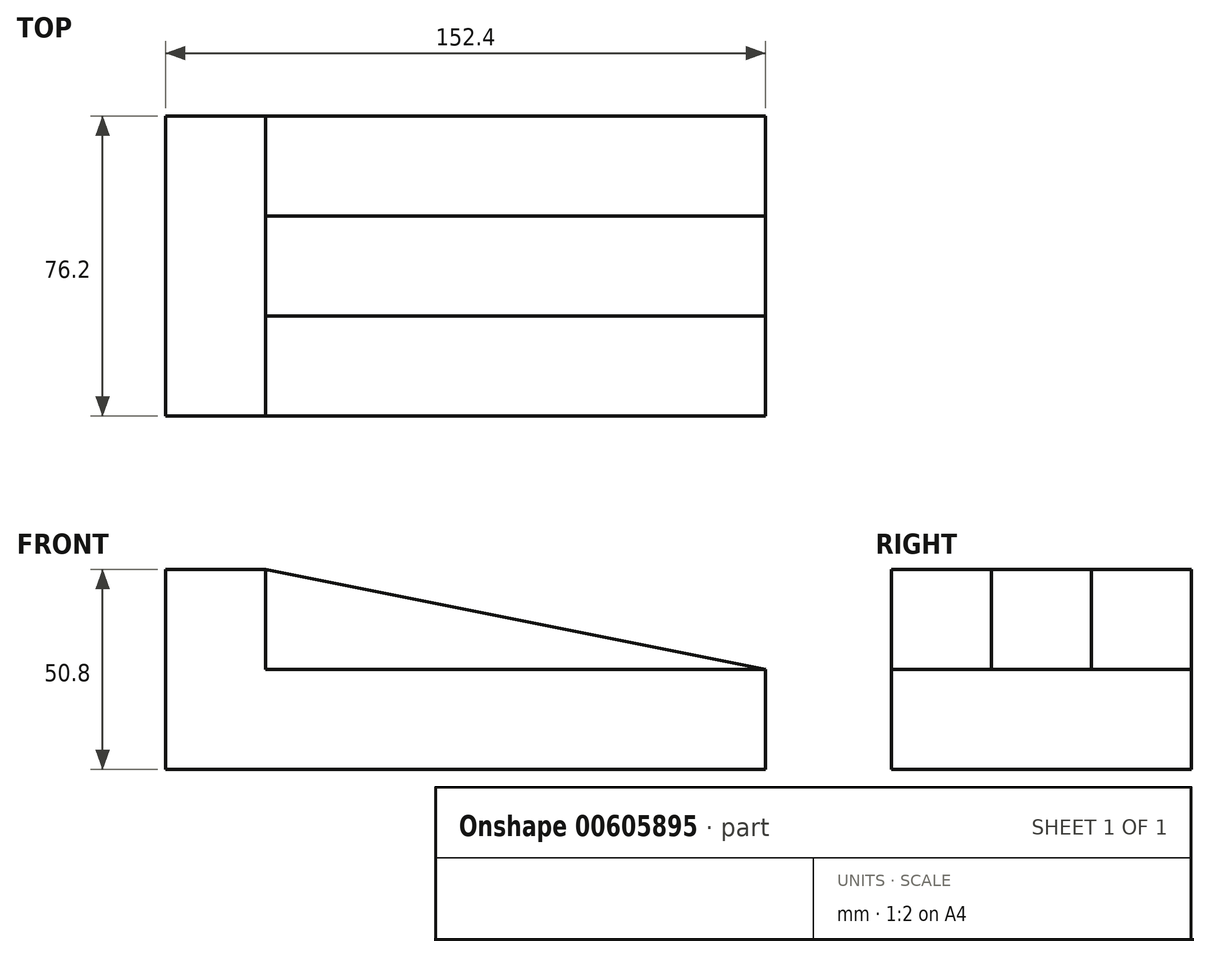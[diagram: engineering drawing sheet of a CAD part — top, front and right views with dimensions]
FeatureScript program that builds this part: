
annotation { "Feature Type Name" : "Feature", "Feature Type Description" : "" }
export const myFeature = defineFeature(function(context is Context, id is Id, definition is map)
    precondition{}
    {
        {
            var Q0;
            Q0=qCreatedBy(makeId("Front.planeOp"),FACE);
            var sketch = newSketch(context, id + "F0", { "sketchPlane" : qUnion([Q0])});
            skLineSegment(sketch, "E0", {"start": v(0, 0) * mm, "end": v(0, 50.8) * mm});
            skLineSegment(sketch, "E1", {"start": v(0, 0) * mm, "end": v(152.4, 0) * mm});
            skLineSegment(sketch, "E2", {"start": v(152.4, 0) * mm, "end": v(152.4, 50.8) * mm});
            skLineSegment(sketch, "E3", {"start": v(152.4, 50.8) * mm, "end": v(0, 50.8) * mm});
            skSolve(sketch);
        }
        {
            var Q0;
            Q0=makeQuery(id+"F0.imprint","IMPRINT",FACE,{"disambiguationData":[TD([[makeQuery(id+"F0.imprint","IMPRINT",EDGE,{"derivedFrom":sQuery(id+"F0.wireOp",EDGE,"E0")}),-1.0]])]});
            extrude(context, id + "F1", {"entities" : qUnion([Q0]), "depth" : 76.2 * mm, "offsetDistance" : 25.4 * mm});
        }
        {
            var Q0;
            Q0=makeQuery(id+"F1.opExtrude","CAP_FACE",FACE,{"disambiguationData":[OSD([sQuery(id+"F0.wireOp",EDGE,"E0"),sQuery(id+"F0.wireOp",EDGE,"E1"),sQuery(id+"F0.wireOp",EDGE,"E2"),sQuery(id+"F0.wireOp",EDGE,"E3")])],"isStart":false});
            var sketch = newSketch(context, id + "F2", { "sketchPlane" : qUnion([Q0])});
            skLineSegment(sketch, "E4", {"start": v(0, 50.8) * mm, "end": v(25.4, 50.8) * mm});
            skLineSegment(sketch, "E5", {"start": v(25.4, 50.8) * mm, "end": v(25.4, 25.4) * mm});
            skLineSegment(sketch, "E6", {"start": v(25.4, 25.4) * mm, "end": v(152.4, 25.4) * mm});
            skLineSegment(sketch, "E7", {"start": v(152.4, 25.4) * mm, "end": v(25.4, 50.8) * mm});
            skSolve(sketch);
        }
        {
            var Q0;
            {var subQ0=sQuery(id+"F2.wireOp",EDGE,"E7");Q0=makeQuery(id+"F2.imprint","IMPRINT",FACE,{"disambiguationData":[TD([[makeQuery(id+"F2.imprint","IMPRINT",EDGE,{"derivedFrom":subQ0}),-1.0]])]});}
            extrude(context, id + "F3", {"entities" : qUnion([Q0]), "operationType" : NewBodyOperationType.REMOVE, "oppositeDirection" : true, "depth" : 76.2 * mm, "offsetDistance" : 25.4 * mm});
        }
        {
            var Q0;
            Q0=makeQuery(id+"F1.opExtrude","CAP_FACE",FACE,{"disambiguationData":[OSD([sQuery(id+"F0.wireOp",EDGE,"E0"),sQuery(id+"F0.wireOp",EDGE,"E1"),sQuery(id+"F0.wireOp",EDGE,"E2"),sQuery(id+"F0.wireOp",EDGE,"E3")])],"isStart":false});
            var sketch = newSketch(context, id + "F4", { "sketchPlane" : qUnion([Q0])});
            skLineSegment(sketch, "E8", {"start": v(25.4, 50.8) * mm, "end": v(25.4, 25.4) * mm});
            skLineSegment(sketch, "E9", {"start": v(25.4, 25.4) * mm, "end": v(152.4, 25.4) * mm});
            skSolve(sketch);
        }
        {
            var Q0;
            Q0=makeQuery(id+"F4.imprint","IMPRINT",FACE,{"disambiguationData":[TD([[makeQuery(id+"F4.imprint","IMPRINT",EDGE,{"derivedFrom":sQuery(id+"F4.wireOp",EDGE,"E8")}),1.0]])]});
            extrude(context, id + "F5", {"entities" : qUnion([Q0]), "operationType" : NewBodyOperationType.REMOVE, "oppositeDirection" : true, "depth" : 25.4 * mm, "offsetDistance" : 25.4 * mm});
        }
        {
            var Q0;
            Q0=makeQuery(id+"F1.opExtrude","CAP_FACE",FACE,{"disambiguationData":[OSD([sQuery(id+"F0.wireOp",EDGE,"E0"),sQuery(id+"F0.wireOp",EDGE,"E1"),sQuery(id+"F0.wireOp",EDGE,"E2"),sQuery(id+"F0.wireOp",EDGE,"E3")])],"isStart":true});
            var sketch = newSketch(context, id + "F6", { "sketchPlane" : qUnion([Q0])});
            skLineSegment(sketch, "E10", {"start": v(-25.4, 50.8) * mm, "end": v(-25.4, 25.4) * mm});
            skLineSegment(sketch, "E11", {"start": v(-25.4, 25.4) * mm, "end": v(-152.4, 25.4) * mm});
            skSolve(sketch);
        }
        {
            var Q0;
            Q0=makeQuery(id+"F6.imprint","IMPRINT",FACE,{"disambiguationData":[TD([[makeQuery(id+"F6.imprint","IMPRINT",EDGE,{"derivedFrom":sQuery(id+"F6.wireOp",EDGE,"E10")}),-1.0]])]});
            extrude(context, id + "F7", {"entities" : qUnion([Q0]), "operationType" : NewBodyOperationType.REMOVE, "oppositeDirection" : true, "depth" : 25.4 * mm, "offsetDistance" : 25.4 * mm});
        }
    });
